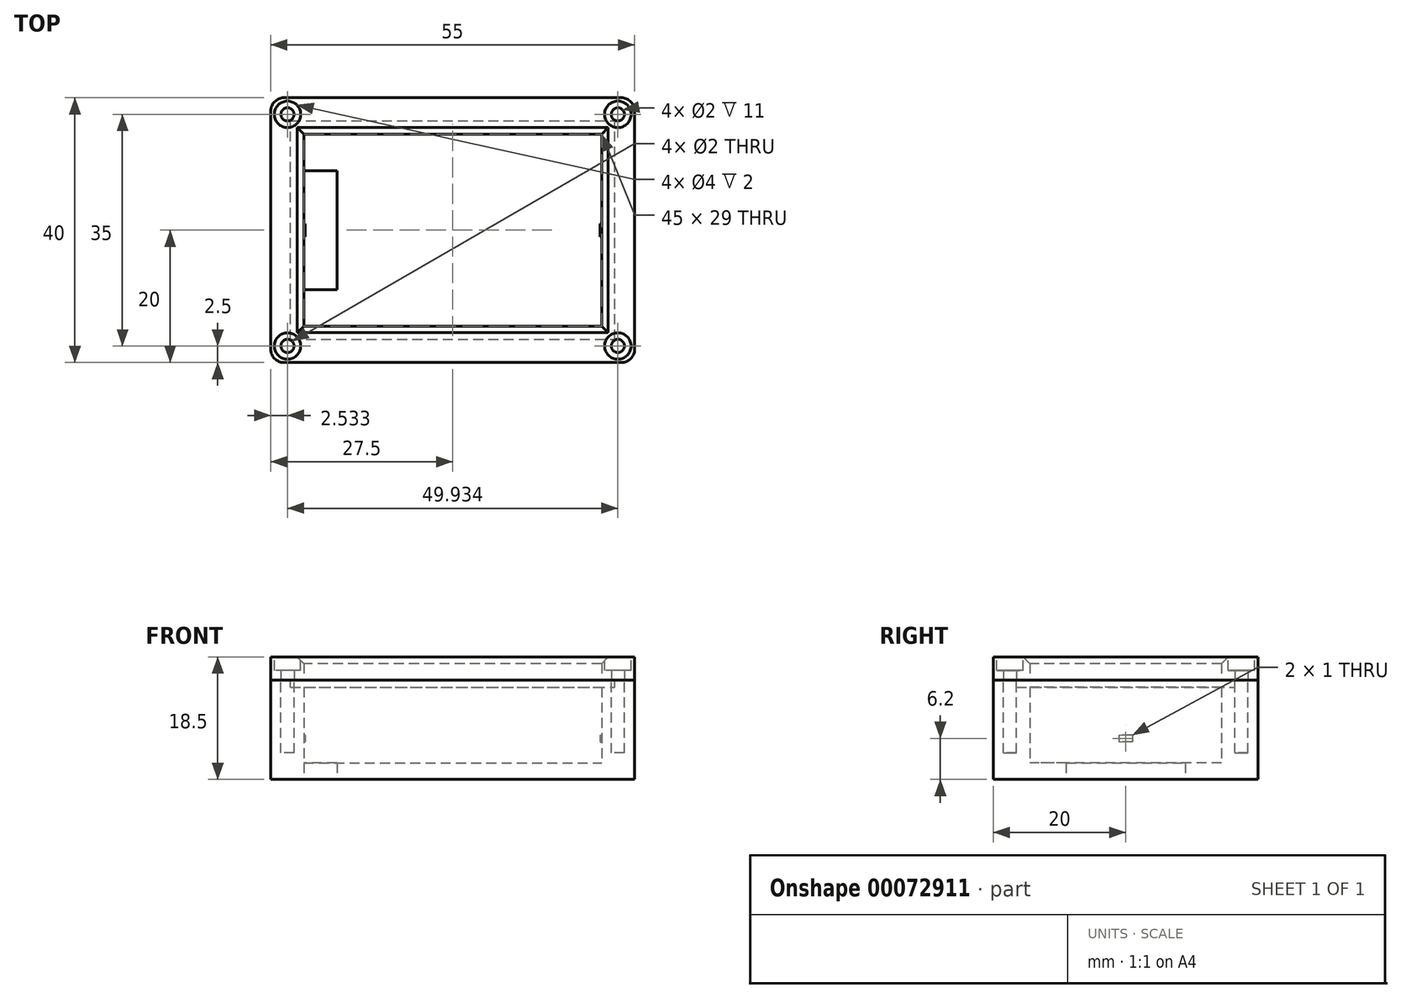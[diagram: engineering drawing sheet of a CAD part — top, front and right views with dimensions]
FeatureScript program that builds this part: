
annotation { "Feature Type Name" : "Feature", "Feature Type Description" : "" }
export const myFeature = defineFeature(function(context is Context, id is Id, definition is map)
    precondition{}
    {
        {
            var Q0;
            Q0=qCreatedBy(makeId("Top.planeOp"),FACE);
            var sketch = newSketch(context, id + "F0", { "sketchPlane" : qUnion([Q0])});
            skLineSegment(sketch, "E0.rect.bottom", {"start": v(-22.5, 14.5) * mm, "end": v(22.5, 14.5) * mm});
            skLineSegment(sketch, "E0.rect.top", {"start": v(-22.5, -14.5) * mm, "end": v(22.5, -14.5) * mm});
            skLineSegment(sketch, "E0.rect.left", {"start": v(-22.5, 14.5) * mm, "end": v(-22.5, -14.5) * mm});
            skLineSegment(sketch, "E0.rect.right", {"start": v(22.5, 14.5) * mm, "end": v(22.5, -14.5) * mm});
            skPoint(sketch, "E0.rect.middle", {"position": v(0, 0) * mm});
            skSolve(sketch);
        }
        {
            var Q0;
            Q0 = qSketchRegion(id + "F0", true);
            extrude(context, id + "F1", {"entities" : qUnion([Q0]), "depth" : 5.7 * mm});
        }
        {
            var Q0;
            Q0=makeQuery(id+"F1.opExtrude","CAP_FACE",FACE,{"disambiguationData":[OSD([sQuery(id+"F0.wireOp",EDGE,"E0.rect.bottom"),sQuery(id+"F0.wireOp",EDGE,"E0.rect.top"),sQuery(id+"F0.wireOp",EDGE,"E0.rect.left"),sQuery(id+"F0.wireOp",EDGE,"E0.rect.right")])],"isStart":false});
            var sketch = newSketch(context, id + "F2", { "sketchPlane" : qUnion([Q0])});
            skLineSegment(sketch, "E1.rect.bottom", {"start": v(-17.05, 12.85) * mm, "end": v(17.05, 12.85) * mm});
            skLineSegment(sketch, "E1.rect.top", {"start": v(-17.05, -12.85) * mm, "end": v(17.05, -12.85) * mm});
            skLineSegment(sketch, "E1.rect.left", {"start": v(-17.05, 12.85) * mm, "end": v(-17.05, -12.85) * mm});
            skLineSegment(sketch, "E1.rect.right", {"start": v(17.05, 12.85) * mm, "end": v(17.05, -12.85) * mm});
            skPoint(sketch, "E1.rect.middle", {"position": v(0, 0) * mm});
            skSolve(sketch);
        }
        {
            var Q0;
            Q0 = qSketchRegion(id + "F2", true);
            extrude(context, id + "F3", {"entities" : qUnion([Q0]), "operationType" : NewBodyOperationType.ADD, "depth" : 7.8 * mm});
        }
        {
            var Q0;
            Q0=makeQuery(id+"F1.opExtrude","CAP_FACE",FACE,{"disambiguationData":[OSD([sQuery(id+"F0.wireOp",EDGE,"E0.rect.bottom"),sQuery(id+"F0.wireOp",EDGE,"E0.rect.top"),sQuery(id+"F0.wireOp",EDGE,"E0.rect.left"),sQuery(id+"F0.wireOp",EDGE,"E0.rect.right")])],"isStart":true});
            extrude(context, id + "F4", {"entities" : qUnion([Q0]), "operationType" : NewBodyOperationType.ADD, "depth" : 6 * mm});
        }
        {
            var Q0;
            Q0=makeQuery(id+"F4.opExtrude","CAP_FACE",FACE,{"disambiguationData":[OSD([sQuery(id+"F0.wireOp",EDGE,"E0.rect.bottom"),sQuery(id+"F0.wireOp",EDGE,"E0.rect.top"),sQuery(id+"F0.wireOp",EDGE,"E0.rect.left"),sQuery(id+"F0.wireOp",EDGE,"E0.rect.right")])],"isStart":false});
            var sketch = newSketch(context, id + "F5", { "sketchPlane" : qUnion([Q0])});
            skLineSegment(sketch, "E2.rect.bottom", {"start": v(-17.5, 9) * mm, "end": v(-22.5, 9) * mm});
            skLineSegment(sketch, "E2.rect.top", {"start": v(-17.5, -9) * mm, "end": v(-22.5, -9) * mm});
            skLineSegment(sketch, "E2.rect.left", {"start": v(-17.5, 9) * mm, "end": v(-17.5, -9) * mm});
            skPoint(sketch, "E2.rect.middle", {"position": v(-22.5, 0) * mm});
            skLineSegment(sketch, "E3", {"start": v(-22.5, 9) * mm, "end": v(-22.5, -9) * mm});
            skPoint(sketch, "E2.rect.right.start.orphan", {"position": v(-27.5, 9) * mm});
            skPoint(sketch, "E4.orphan", {"position": v(-27.5, -9) * mm});
            skSolve(sketch);
        }
        {
            var Q0;
            {var subQ5=sQuery(id+"F5.wireOp",EDGE,"E2.rect.bottom");Q0=makeQuery(id+"F5.imprint","IMPRINT",FACE,{"disambiguationData":[TD([[makeQuery(id+"F5.imprint","IMPRINT",EDGE,{"derivedFrom":subQ5}),-1.0]])]});}
            extrude(context, id + "F6", {"entities" : qUnion([Q0]), "operationType" : NewBodyOperationType.REMOVE, "oppositeDirection" : true, "depth" : 4 * mm});
        }
        {
            var Q0;
            Q0=makeQuery(id+"F3.opExtrude","CAP_FACE",FACE,{"disambiguationData":[OSD([sQuery(id+"F2.wireOp",EDGE,"E1.rect.bottom"),sQuery(id+"F2.wireOp",EDGE,"E1.rect.top"),sQuery(id+"F2.wireOp",EDGE,"E1.rect.left"),sQuery(id+"F2.wireOp",EDGE,"E1.rect.right")])],"isStart":false});
            cPlane(context, id + "F7", {"entities" : qUnion([Q0]), "cplaneType" : CPlaneType.OFFSET, "offset" : 2 * mm, "width" : 150 * mm, "height" : 150 * mm});
        }
        {
            var Q0;
            Q0=qCreatedBy(id+"F7.planeOp",FACE);
            var sketch = newSketch(context, id + "F8", { "sketchPlane" : qUnion([Q0])});
            skLineSegment(sketch, "E5.rect.bottom", {"start": v(27.5, -20) * mm, "end": v(-27.5, -20) * mm});
            skLineSegment(sketch, "E5.rect.top", {"start": v(27.5, 20) * mm, "end": v(-27.5, 20) * mm});
            skLineSegment(sketch, "E5.rect.left", {"start": v(27.5, -20) * mm, "end": v(27.5, 20) * mm});
            skLineSegment(sketch, "E5.rect.right", {"start": v(-27.5, -20) * mm, "end": v(-27.5, 20) * mm});
            skPoint(sketch, "E5.rect.middle", {"position": v(0, 0) * mm});
            skSolve(sketch);
        }
        {
            var Q0;
            Q0 = qSketchRegion(id + "F8", true);
            extrude(context, id + "F9", {"entities" : qUnion([Q0]), "oppositeDirection" : true, "depth" : 20 * mm});
        }
        {
            var Q0;
            Q0=makeQuery(id+"F1.opExtrude","SWEPT_BODY",BODY,{"disambiguationData":[OSD([sQuery(id+"F0.wireOp",EDGE,"E0.rect.bottom"),sQuery(id+"F0.wireOp",EDGE,"E0.rect.top"),sQuery(id+"F0.wireOp",EDGE,"E0.rect.left"),sQuery(id+"F0.wireOp",EDGE,"E0.rect.right")])]});
            var Q1;
            Q1=makeQuery(id+"F9.opExtrude","SWEPT_BODY",BODY,{"disambiguationData":[OSD([sQuery(id+"F8.wireOp",EDGE,"E5.rect.bottom"),sQuery(id+"F8.wireOp",EDGE,"E5.rect.top"),sQuery(id+"F8.wireOp",EDGE,"E5.rect.left"),sQuery(id+"F8.wireOp",EDGE,"E5.rect.right")])]});
            booleanBodies(context, id + "F10", {"operationType" : BooleanOperationType.SUBTRACTION, "tools" : qUnion([Q0]), "targets" : qUnion([Q1])});
        }
        {
            var Q0;
            Q0=makeQuery(id+"F9.opExtrude","CAP_FACE",FACE,{"disambiguationData":[OSD([sQuery(id+"F8.wireOp",EDGE,"E5.rect.bottom"),sQuery(id+"F8.wireOp",EDGE,"E5.rect.top"),sQuery(id+"F8.wireOp",EDGE,"E5.rect.left"),sQuery(id+"F8.wireOp",EDGE,"E5.rect.right")])],"isStart":true});
            var sketch = newSketch(context, id + "F11", { "sketchPlane" : qUnion([Q0])});
            skLineSegment(sketch, "E6.0", {"start": v(-22.5, 14.5) * mm, "end": v(22.5, 14.5) * mm});
            skLineSegment(sketch, "E7.0", {"start": v(-22.5, 14.5) * mm, "end": v(-22.5, -14.5) * mm});
            skLineSegment(sketch, "E8.0", {"start": v(22.5, 14.5) * mm, "end": v(22.5, -14.5) * mm});
            skLineSegment(sketch, "E9.0", {"start": v(-22.5, -14.5) * mm, "end": v(22.5, -14.5) * mm});
            skSolve(sketch);
        }
        {
            var Q0;
            Q0 = qSketchRegion(id + "F11", true);
            var Q1;
            Q1=makeQuery(id+"F10.opBoolean","COPY",FACE,{"derivedFrom":makeQuery(id+"F1.opExtrude","CAP_FACE",FACE,{"disambiguationData":[OSD([sQuery(id+"F0.wireOp",EDGE,"E0.rect.bottom"),sQuery(id+"F0.wireOp",EDGE,"E0.rect.top"),sQuery(id+"F0.wireOp",EDGE,"E0.rect.left"),sQuery(id+"F0.wireOp",EDGE,"E0.rect.right")])],"isStart":false})});
            extrude(context, id + "F12", {"entities" : qUnion([Q0]), "operationType" : NewBodyOperationType.REMOVE, "endBound" : BoundingType.UP_TO_SURFACE, "oppositeDirection" : true, "endBoundEntityFace" : qUnion([Q1]), "depth" : 25 * mm});
        }
        {
            var Q0;
            {var subQ0=sQuery(id+"F0.wireOp",EDGE,"E0.rect.right");Q0=makeQuery(id+"F12.boolean.opBoolean","MERGE",FACE,{"derivedFrom":[makeQuery(id+"F10.opBoolean","COPY",FACE,{"derivedFrom":makeQuery(id+"F4.boolean.opBoolean","MERGE",FACE,{"derivedFrom":[makeQuery(id+"F1.opExtrude","SWEPT_FACE",FACE,{"disambiguationData":[OSD([subQ0])]}),makeQuery(id+"F4.opExtrude","SWEPT_FACE",FACE,{"disambiguationData":[OSD([subQ0])]})]})}),makeQuery(id+"F12.opExtrude","SWEPT_FACE",FACE,{"disambiguationData":[OSD([sQuery(id+"F11.wireOp",EDGE,"E8.0")])]})]});}
            var sketch = newSketch(context, id + "F13", { "sketchPlane" : qUnion([Q0])});
            skPoint(sketch, "E10.endSnap0", {"position": v(0, -2) * mm});
            skLineSegment(sketch, "E11.rect.bottom", {"start": v(-1, 2.2) * mm, "end": v(1, 2.2) * mm});
            skLineSegment(sketch, "E11.rect.left", {"start": v(-1, 2.2) * mm, "end": v(-1, 1.2) * mm});
            skLineSegment(sketch, "E11.rect.right", {"start": v(1, 2.2) * mm, "end": v(1, 1.2) * mm});
            skPoint(sketch, "E11.rect.middle", {"position": v(0, 1.2) * mm});
            skPoint(sketch, "E12.orphan", {"position": v(-1, 0.2) * mm});
            skPoint(sketch, "E13.orphan", {"position": v(1, 0.2) * mm});
            skPoint(sketch, "E10.start.orphan", {"position": v(0, -2) * mm});
            skLineSegment(sketch, "E14", {"start": v(-1, 1.2) * mm, "end": v(1, 1.2) * mm});
            skSolve(sketch);
        }
        {
            var Q0;
            Q0 = qSketchRegion(id + "F13", true);
            extrude(context, id + "F14", {"entities" : qUnion([Q0]), "depth" : 0.2 * mm});
        }
        {
            var Q0;
            Q0=makeQuery(id+"F14.opExtrude","SWEPT_BODY",BODY,{"disambiguationData":[OSD([sQuery(id+"F13.wireOp",EDGE,"E11.rect.bottom"),sQuery(id+"F13.wireOp",EDGE,"E11.rect.left"),sQuery(id+"F13.wireOp",EDGE,"E11.rect.right"),sQuery(id+"F13.wireOp",EDGE,"E14")])]});
            var Q1;
            Q1=qCreatedBy(makeId("Right.planeOp"),FACE);
            mirror(context, id + "F15", {"operationType" : NewBodyOperationType.ADD, "entities" : qUnion([Q0]), "mirrorPlane" : qUnion([Q1])});
        }
        {
            var Q0;
            Q0 = qSketchRegion(id + "F8", true);
            extrude(context, id + "F16", {"entities" : qUnion([Q0]), "operationType" : NewBodyOperationType.REMOVE, "oppositeDirection" : true, "depth" : 5 * mm});
        }
        {
            var Q0;
            Q0=makeQuery(id+"F16.boolean.opBoolean","COPY",FACE,{"derivedFrom":makeQuery(id+"F16.opExtrude","CAP_FACE",FACE,{"disambiguationData":[OSD([sQuery(id+"F8.wireOp",EDGE,"E5.rect.bottom"),sQuery(id+"F8.wireOp",EDGE,"E5.rect.top"),sQuery(id+"F8.wireOp",EDGE,"E5.rect.left"),sQuery(id+"F8.wireOp",EDGE,"E5.rect.right")])],"isStart":false})});
            var sketch = newSketch(context, id + "F17", { "sketchPlane" : qUnion([Q0])});
            skLineSegment(sketch, "E15.rect.bottom", {"start": v(-24.5, -16.5) * mm, "end": v(24.5, -16.5) * mm});
            skLineSegment(sketch, "E15.rect.top", {"start": v(-24.5, 16.5) * mm, "end": v(24.5, 16.5) * mm});
            skLineSegment(sketch, "E15.rect.left", {"start": v(-24.5, -16.5) * mm, "end": v(-24.5, 16.5) * mm});
            skLineSegment(sketch, "E15.rect.right", {"start": v(24.5, -16.5) * mm, "end": v(24.5, 16.5) * mm});
            skPoint(sketch, "E15.rect.middle", {"position": v(0, 0) * mm});
            skSolve(sketch);
        }
        {
            var Q0;
            Q0=makeQuery(id+"F17.imprint","IMPRINT",FACE,{"disambiguationData":[TD([[makeQuery(id+"F17.imprint","IMPRINT",EDGE,{"derivedFrom":sQuery(id+"F17.wireOp",EDGE,"E15.rect.bottom")}),1.0]])]});
            extrude(context, id + "F18", {"entities" : qUnion([Q0]), "operationType" : NewBodyOperationType.REMOVE, "oppositeDirection" : true, "depth" : 1.1 * mm});
        }
        {
            var Q0;
            Q0=makeQuery(id+"F16.boolean.opBoolean","COPY",FACE,{"derivedFrom":makeQuery(id+"F16.opExtrude","CAP_FACE",FACE,{"disambiguationData":[OSD([sQuery(id+"F8.wireOp",EDGE,"E5.rect.bottom"),sQuery(id+"F8.wireOp",EDGE,"E5.rect.top"),sQuery(id+"F8.wireOp",EDGE,"E5.rect.left"),sQuery(id+"F8.wireOp",EDGE,"E5.rect.right")])],"isStart":false})});
            var sketch = newSketch(context, id + "F19", { "sketchPlane" : qUnion([Q0])});
            skCircle(sketch, "E16", {"center": v(-24.97, -17.5) * mm, "radius": 1 * mm});
            skLineSegment(sketch, "E17", {"start": v(-38.7, 0) * mm, "end": v(45.6, 0) * mm, "construction": true});
            skPoint(sketch, "E17.endSnap0", {"position": v(-24.5, 0) * mm});
            skLineSegment(sketch, "E18", {"start": v(0, -38.73) * mm, "end": v(0, 46.85) * mm, "construction": true});
            skPoint(sketch, "E18.endSnap0", {"position": v(0, 20) * mm});
            skCircle(sketch, "E19.MirrorC", {"center": v(-24.97, 17.5) * mm, "radius": 1 * mm});
            skCircle(sketch, "E20.MirrorC", {"center": v(24.97, -17.5) * mm, "radius": 1 * mm});
            skCircle(sketch, "E21.MirrorC", {"center": v(24.97, 17.5) * mm, "radius": 1 * mm});
            skSolve(sketch);
        }
        {
            var Q0;
            Q0 = qSketchRegion(id + "F19", true);
            extrude(context, id + "F20", {"entities" : qUnion([Q0]), "operationType" : NewBodyOperationType.REMOVE, "oppositeDirection" : true, "depth" : 11 * mm});
        }
        {
            var Q0;
            Q0=makeQuery(id+"F16.boolean.opBoolean","COPY",FACE,{"derivedFrom":makeQuery(id+"F16.opExtrude","CAP_FACE",FACE,{"disambiguationData":[OSD([sQuery(id+"F8.wireOp",EDGE,"E5.rect.bottom"),sQuery(id+"F8.wireOp",EDGE,"E5.rect.top"),sQuery(id+"F8.wireOp",EDGE,"E5.rect.left"),sQuery(id+"F8.wireOp",EDGE,"E5.rect.right")])],"isStart":false})});
            var sketch = newSketch(context, id + "F21", { "sketchPlane" : qUnion([Q0])});
            skLineSegment(sketch, "E22.0", {"start": v(27.5, 20) * mm, "end": v(-27.5, 20) * mm});
            skLineSegment(sketch, "E23.0", {"start": v(-27.5, -20) * mm, "end": v(-27.5, 20) * mm});
            skLineSegment(sketch, "E24.0", {"start": v(-22.5, 14.5) * mm, "end": v(-22.5, -14.5) * mm});
            skLineSegment(sketch, "E25.0", {"start": v(-22.5, 14.5) * mm, "end": v(22.5, 14.5) * mm});
            skLineSegment(sketch, "E26.0", {"start": v(-22.5, -14.5) * mm, "end": v(22.5, -14.5) * mm});
            skLineSegment(sketch, "E27.0", {"start": v(27.5, -20) * mm, "end": v(-27.5, -20) * mm});
            skLineSegment(sketch, "E28.0", {"start": v(22.5, 14.5) * mm, "end": v(22.5, -14.5) * mm});
            skLineSegment(sketch, "E29.0", {"start": v(27.5, -20) * mm, "end": v(27.5, 20) * mm});
            skCircle(sketch, "E30.0", {"center": v(-24.97, 17.5) * mm, "radius": 1 * mm});
            skCircle(sketch, "E31.0", {"center": v(-24.97, -17.5) * mm, "radius": 1 * mm});
            skCircle(sketch, "E32.0", {"center": v(24.97, 17.5) * mm, "radius": 1 * mm});
            skCircle(sketch, "E33.0", {"center": v(24.97, -17.5) * mm, "radius": 1 * mm});
            skSolve(sketch);
        }
        {
            var Q0;
            Q0 = qSketchRegion(id + "F21", true);
            extrude(context, id + "F22", {"entities" : qUnion([Q0]), "depth" : 3.5 * mm});
        }
        {
            var Q0;
            Q0=makeQuery(id+"F22.opExtrude","CAP_FACE",FACE,{"disambiguationData":[OSD([sQuery(id+"F21.wireOp",EDGE,"E22.0"),sQuery(id+"F21.wireOp",EDGE,"E23.0"),sQuery(id+"F21.wireOp",EDGE,"E24.0"),sQuery(id+"F21.wireOp",EDGE,"E25.0"),sQuery(id+"F21.wireOp",EDGE,"E26.0"),sQuery(id+"F21.wireOp",EDGE,"E27.0"),sQuery(id+"F21.wireOp",EDGE,"E28.0"),sQuery(id+"F21.wireOp",EDGE,"E29.0"),sQuery(id+"F21.wireOp",EDGE,"E30.0"),sQuery(id+"F21.wireOp",EDGE,"E31.0"),sQuery(id+"F21.wireOp",EDGE,"E32.0"),sQuery(id+"F21.wireOp",EDGE,"E33.0")])],"isStart":false});
            var sketch = newSketch(context, id + "F23", { "sketchPlane" : qUnion([Q0])});
            skPoint(sketch, "E34.0", {"position": v(24.97, 17.5) * mm});
            skCircle(sketch, "E35", {"center": v(24.97, 17.5) * mm, "radius": 2 * mm});
            skLineSegment(sketch, "E36", {"start": v(35.48, 0) * mm, "end": v(-41.07, 0) * mm, "construction": true});
            skLineSegment(sketch, "E37", {"start": v(0, 34.93) * mm, "end": v(0, -48.03) * mm, "construction": true});
            skCircle(sketch, "E38.MirrorC", {"center": v(24.97, -17.5) * mm, "radius": 2 * mm});
            skCircle(sketch, "E39.MirrorC", {"center": v(-24.97, 17.5) * mm, "radius": 2 * mm});
            skCircle(sketch, "E40.MirrorC", {"center": v(-24.97, -17.5) * mm, "radius": 2 * mm});
            skSolve(sketch);
        }
        {
            var Q0;
            Q0 = qSketchRegion(id + "F23", true);
            extrude(context, id + "F24", {"entities" : qUnion([Q0]), "operationType" : NewBodyOperationType.REMOVE, "oppositeDirection" : true, "depth" : 2 * mm});
        }
        {
            var Q0;
            Q0=makeQuery(id+"F9.opExtrude","SWEPT_EDGE",EDGE,{"disambiguationData":[OSD([sQuery(id+"F8.wireOp",EDGE,"E5.rect.top"),sQuery(id+"F8.wireOp",EDGE,"E5.rect.right")])]});
            var Q1;
            Q1=makeQuery(id+"F22.opExtrude","SWEPT_EDGE",EDGE,{"disambiguationData":[OSD([sQuery(id+"F21.wireOp",EDGE,"E22.0"),sQuery(id+"F21.wireOp",EDGE,"E23.0")])]});
            var Q2;
            Q2=makeQuery(id+"F22.opExtrude","SWEPT_EDGE",EDGE,{"disambiguationData":[OSD([sQuery(id+"F21.wireOp",EDGE,"E23.0"),sQuery(id+"F21.wireOp",EDGE,"E27.0")])]});
            var Q3;
            Q3=makeQuery(id+"F9.opExtrude","SWEPT_EDGE",EDGE,{"disambiguationData":[OSD([sQuery(id+"F8.wireOp",EDGE,"E5.rect.bottom"),sQuery(id+"F8.wireOp",EDGE,"E5.rect.right")])]});
            var Q4;
            Q4=makeQuery(id+"F22.opExtrude","SWEPT_EDGE",EDGE,{"disambiguationData":[OSD([sQuery(id+"F21.wireOp",EDGE,"E27.0"),sQuery(id+"F21.wireOp",EDGE,"E29.0")])]});
            var Q5;
            Q5=makeQuery(id+"F9.opExtrude","SWEPT_EDGE",EDGE,{"disambiguationData":[OSD([sQuery(id+"F8.wireOp",EDGE,"E5.rect.bottom"),sQuery(id+"F8.wireOp",EDGE,"E5.rect.left")])]});
            var Q6;
            Q6=makeQuery(id+"F22.opExtrude","SWEPT_EDGE",EDGE,{"disambiguationData":[OSD([sQuery(id+"F21.wireOp",EDGE,"E22.0"),sQuery(id+"F21.wireOp",EDGE,"E29.0")])]});
            var Q7;
            Q7=makeQuery(id+"F9.opExtrude","SWEPT_EDGE",EDGE,{"disambiguationData":[OSD([sQuery(id+"F8.wireOp",EDGE,"E5.rect.top"),sQuery(id+"F8.wireOp",EDGE,"E5.rect.left")])]});
            fillet(context, id + "F25", {"entities" : qUnion([Q0, Q1, Q2, Q3, Q4, Q5, Q6, Q7]), "radius" : 2 * mm, "tangentPropagation" : true, "allowEdgeOverflow" : false});
        }
        {
            var Q0;
            Q0=makeQuery(id+"F22.opExtrude","CAP_EDGE",EDGE,{"disambiguationData":[OSD([sQuery(id+"F21.wireOp",EDGE,"E26.0")])],"isStart":false});
            var Q1;
            Q1=makeQuery(id+"F22.opExtrude","CAP_EDGE",EDGE,{"disambiguationData":[OSD([sQuery(id+"F21.wireOp",EDGE,"E28.0")])],"isStart":false});
            var Q2;
            Q2=makeQuery(id+"F22.opExtrude","CAP_EDGE",EDGE,{"disambiguationData":[OSD([sQuery(id+"F21.wireOp",EDGE,"E25.0")])],"isStart":false});
            var Q3;
            Q3=makeQuery(id+"F22.opExtrude","CAP_EDGE",EDGE,{"disambiguationData":[OSD([sQuery(id+"F21.wireOp",EDGE,"E24.0")])],"isStart":false});
            chamfer(context, id + "F26", {"entities" : qUnion([Q0, Q1, Q2, Q3]), "width" : 1 * mm, "tangentPropagation" : true});
        }
    });
